# Revit family: 3644
name_source: partatom
category: Plumbing Fixtures
units: mm (PartAtom-declared; Revit-internal decimal feet)

## family parameters
Cut with Voids When Loaded = No
Host = Face
Maintain Annotation Orientation = No
OmniClass Number = 23.65.70.14
OmniClass Title = Fountains
Part Type = Normal
Room Calculation Point = No
Round Connector Dimension = Use Diameter
Shared = Yes

## types (2) — shared parameters
-H Hand Operation = No
-JH31 31” ADA/CBC Children’s Rim Height (30-1/2” for -2 On-Floor, Wall Outlet) = No
-OBC 33” Rim Height (Ontario Building Code) Note: Sensor Operation Only = No
-PDM Metering Liquid Soap Dispenser = No
-PPZ Programmable Piezo Button Electronic Metering = No
-SO Sensor Operation = No
-SO-BAT Sensor Operation, Battery Powered (Batteries Not Included) = No
-ST Single Temperature Supply = No
ADA Compliant = Yes
Assembly Code = D2010600
Basin Shape = D-Shaped
Body Material = Polymer_Resin-Acorn-Corterra-Solid_Surface
CW Connection = Yes
CWFU = 1.5
Cold Water Connection Diameter = 1/2"
Cold Water Connection Radius = 1/4"
Cold Water Connection Width = 3 1/2"
Corterra Color Options = No
Default Elevation = 33 1/2"
Description = Perfect for institutional, commercial and public applications, this four-station hand washing fountain is made from design-flexible cast solid surface Corterra®. This material is sleek, sturdy and ensures long-lasting universal aesthetics. The wash fountain features a wall-mount and is available in off-floor and on-floor configurations.
Flow Rate = 0.5 GPM
HW Connection = Yes
HWFU = 1.5
Height = 40"
Hot Water Connection Diameter = 1/2"
Hot Water Connection Radius = 1/4"
Hot Water Connection Width = 1 1/2"
IAPMO Compliance = IAPMO IGC 156, CSA B45 Series, ASME A112.18.1/CSA B125.1
Installation Type = Wall Mounted
Length = 46"
Manufacturer = Acorn Engineering
Material = Metal-Acorn-Stainless_Steel
Price = Prices may vary. Please consult Manufacturer Representative for most up-to-date price list.
Product Documentation Link = https://www.acorneng.com
Product Page URL = https://www.acorneng.com
URL = https://www.acorneng.com
Vent Connection = No
WFU = 2
Warranty Information URL = https://www.acorneng.com
Waste Connection = Yes
Waste Connection Diameter = 1 1/2"
Waste Connection Height = 24"
Waste Connection Radius = 3/4"
Width = 26"

## per-type parameters (varying)
| type | -1 Off-Floor, Wall Outlet | -2 On-Floor, Wall Outlet | Cold Water Connection Height |
| 3644-1-SO | Yes | No | 17" |
| 3644-2-SO | No | Yes | 12 1/2" |

note: column(s) folded — value = type name in every type: Model

## geometry (parser evidence)
native form markers: Sweep x1
no freeform markers — native parametric forms only
